# Revit family: Crealco Skyline Heavy Duty Sash Top Hung G
name_source: partatom
category: Windows
revit_build: Autodesk Revit 2014 (Build: 20130308_1515(x64)
units: mm (PartAtom-declared; Revit-internal decimal feet)

## types (12) — shared parameters
Corrected Mullion Configuration = 2 mm  [stored 0.00656168 ft]
Custom Window Height = 1190 mm  [stored 3.9042 ft]
Description = Top Hung Type G Standard Sash Window
Frame Profile Thickness = 41 mm  [stored 0.134514 ft]
Heavy Duty Sash = Yes
Limit Fixed Pane Height Max = 3000 mm  [stored 9.84252 ft]
Limit Fixed Pane Height Min = 200 mm  [stored 0.656168 ft]
Limit Fixed Pane Width Max = 3000 mm  [stored 9.84252 ft]
Limit Fixed Pane Width Min = 200 mm  [stored 0.656168 ft]
Limit Sash Height Max = 1200 mm  [stored 3.93701 ft]
Limit Sash Height Min = 300 mm  [stored 0.984252 ft]
Limit Sash Width Max = 1500 mm  [stored 4.92126 ft]
Limit Sash Width Min = 300 mm  [stored 0.984252 ft]
Manufacturer = Crealco
Max System DG Unit Thickness = 25 mm  [stored 0.082021 ft]
Model = Skyline
Rough Width = 3 mm  [stored 0.00984252 ft]
Sash Side Gap = 44 mm
Standard Mullion Different = No
Standard Sash = No
URL = www.crealco.co.za
Wall Closure = By host
zero-valued in all types: Custom Frame Offset From Exterior

## per-type parameters (varying)
| type | Clearvue Insulated LowE SHGC Value | Clearvue Insulated LowE U Value | Clearvue Insulated SHGC Value | Clearvue Insulated U Value | Clearvue SHGC Value | Clearvue U Value | Custom Sash Width | Custom Windload | Custom Window Width | Energy Advantage SHGC Value | Energy Advantage U Value | Intruderprufe Insulated LowE SHGC Value | Intruderprufe Insulated LowE U Value | Intruderprufe Insulated SHGC Value | Intruderprufe Insulated U Value | Intruderprufe LowE SHGC Value | Intruderprufe LowE U Value | Intruderprufe SHGC Value | Intruderprufe U Value | Toughened Safety SHGC Value | Toughened Safety U Value |
| 1200 x 1200mm 1000Pa | 0.712 | 4.29 | 0.712 | 4.36 | 0.545 | 6.05 | 525 mm | 1000 mm  [stored 3.28084 ft] | 1190 mm  [stored 3.9042 ft] | 0.489 | 4.71 | 0.592 | 3.11 | 0.593 | 3.33 | 0.455 | 4.56 | 0.513 | 5.77 | 0.545 | 6.05 |
| 1200 x 1200mm 1500Pa | 0.712 | 4.29 | 0.712 | 4.36 | 0.545 | 6.05 | 525 mm | 1500 mm  [stored 4.92126 ft] | 1190 mm  [stored 3.9042 ft] | 0.489 | 4.71 | 0.592 | 3.11 | 0.593 | 3.33 | 0.455 | 4.56 | 0.513 | 5.77 | 0.545 | 6.05 |
| 1200 x 1200mm 2000Pa | 0.712 | 4.29 | 0.712 | 4.36 | 0.545 | 6.05 | 525 mm | 2000 mm  [stored 6.56168 ft] | 1190 mm  [stored 3.9042 ft] | 0.489 | 4.71 | 0.592 | 3.11 | 0.593 | 3.33 | 0.455 | 4.56 | 0.513 | 5.77 | 0.545 | 6.05 |
| 1500 x 1200mm 1000Pa | 0.74 | 4.48 | 0.74 | 4.54 | 0.591 | 6.03 | 525 mm | 1000 mm  [stored 3.28084 ft] | 1490 mm  [stored 4.88845 ft] | 0.53 | 4.57 | 0.615 | 3.13 | 0.616 | 3.31 | 0.492 | 4.43 | 0.556 | 5.77 | 0.591 | 6.03 |
| 1500 x 1200mm 1500Pa | 0.74 | 4.48 | 0.74 | 4.54 | 0.591 | 6.03 | 525 mm | 1500 mm  [stored 4.92126 ft] | 1490 mm  [stored 4.88845 ft] | 0.53 | 4.57 | 0.615 | 3.13 | 0.616 | 3.31 | 0.492 | 4.43 | 0.556 | 5.77 | 0.591 | 6.03 |
| 1500 x 1200mm 2000Pa | 0.74 | 4.48 | 0.74 | 4.54 | 0.591 | 6.03 | 525 mm | 2000 mm  [stored 6.56168 ft] | 1490 mm  [stored 4.88845 ft] | 0.53 | 4.57 | 0.615 | 3.13 | 0.616 | 3.31 | 0.492 | 4.43 | 0.556 | 5.77 | 0.591 | 6.03 |
| 1800 x 1200mm 1000Pa | 0.739 | 4.5 | 0.739 | 4.55 | 0.595 | 6.03 | 825 mm | 1000 mm  [stored 3.28084 ft] | 1790 mm  [stored 5.8727 ft] | 0.533 | 4.51 | 0.614 | 3.13 | 0.615 | 3.36 | 0.496 | 4.38 | 0.56 | 5.74 | 0.595 | 6.03 |
| 1800 x 1200mm 1500Pa | 0.739 | 4.5 | 0.739 | 4.55 | 0.595 | 6.03 | 825 mm | 1500 mm  [stored 4.92126 ft] | 1790 mm  [stored 5.8727 ft] | 0.533 | 4.51 | 0.614 | 3.13 | 0.615 | 3.36 | 0.496 | 4.38 | 0.56 | 5.74 | 0.595 | 6.03 |
| 1800 x 1200mm 2000Pa | 0.739 | 4.5 | 0.739 | 4.55 | 0.595 | 6.03 | 825 mm | 2000 mm  [stored 6.56168 ft] | 1790 mm  [stored 5.8727 ft] | 0.533 | 4.51 | 0.614 | 3.13 | 0.615 | 3.36 | 0.496 | 4.38 | 0.56 | 5.74 | 0.595 | 6.03 |
| 2400 x 1200mm 1000Pa | 0.767 | 4.69 | 0.767 | 4.73 | 0.639 | 6.01 | 825 mm | 1000 mm  [stored 3.28084 ft] | 2390 mm  [stored 7.84121 ft] | 0.572 | 4.39 | 0.637 | 3.16 | 0.638 | 3.33 | 0.532 | 4.26 | 0.601 | 5.74 | 0.639 | 6.01 |
| 2400 x 1200mm 1500Pa | 0.767 | 4.69 | 0.767 | 4.73 | 0.639 | 6.01 | 825 mm | 1500 mm  [stored 4.92126 ft] | 2390 mm  [stored 7.84121 ft] | 0.572 | 4.39 | 0.637 | 3.16 | 0.638 | 3.33 | 0.532 | 4.26 | 0.601 | 5.74 | 0.639 | 6.01 |
| 2400 x 1200mm 2000Pa | 0.767 | 4.69 | 0.767 | 4.73 | 0.639 | 6.01 | 825 mm | 2000 mm  [stored 6.56168 ft] | 2390 mm  [stored 7.84121 ft] | 0.572 | 4.39 | 0.637 | 3.16 | 0.638 | 3.33 | 0.532 | 4.26 | 0.601 | 5.74 | 0.639 | 6.01 |

note: [stored X ft] marks values corroborated as IEEE doubles in the binary element streams (Revit-internal decimal feet)

## geometry (parser evidence)
native form markers: Sweep x14
no freeform markers — native parametric forms only
